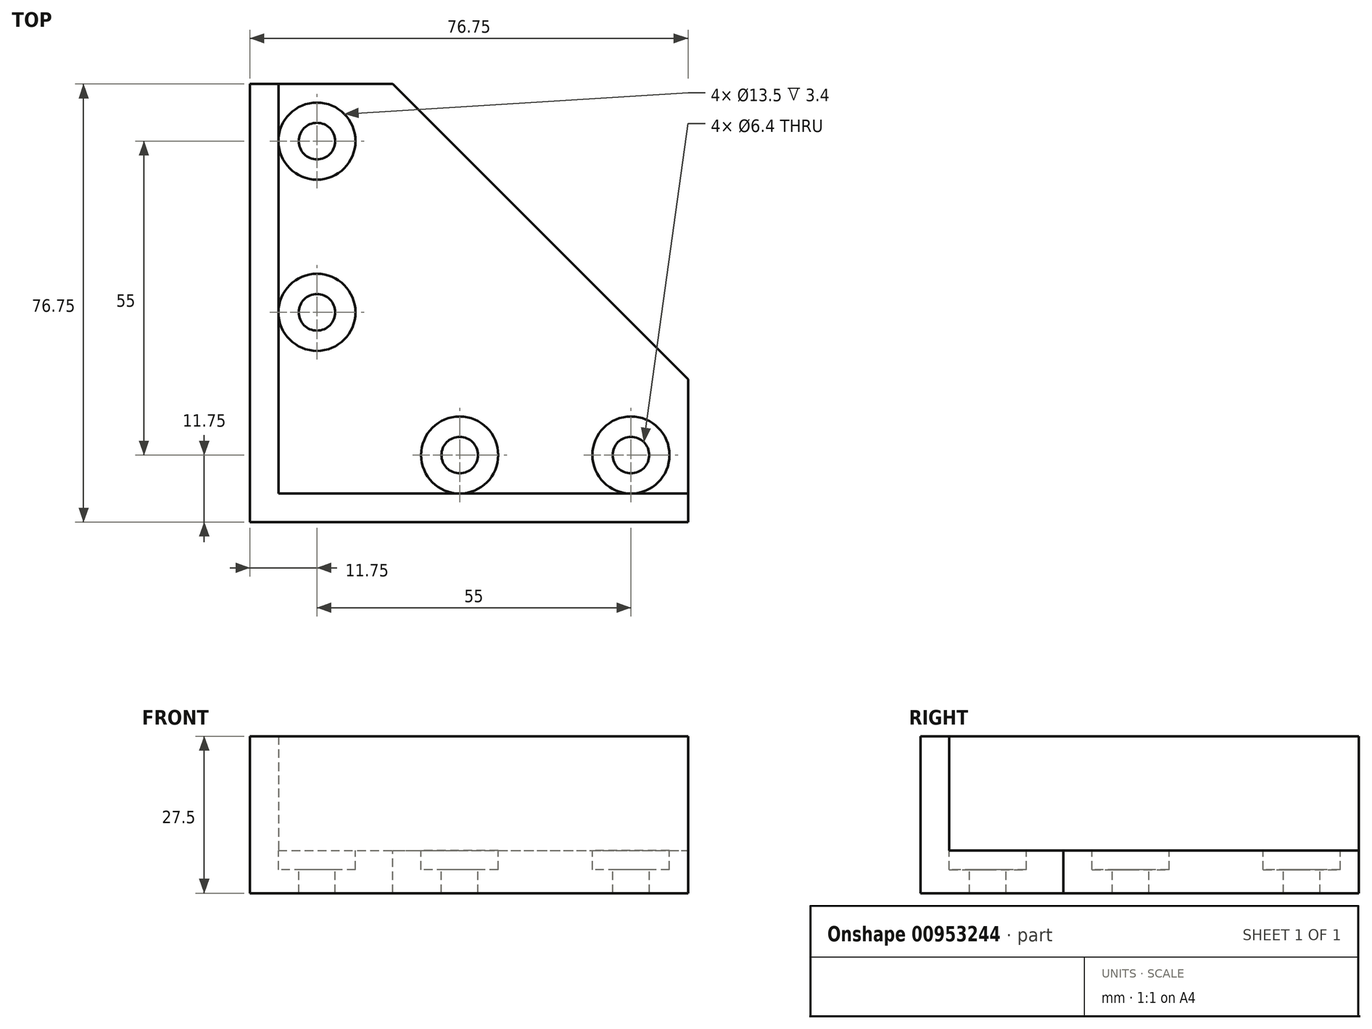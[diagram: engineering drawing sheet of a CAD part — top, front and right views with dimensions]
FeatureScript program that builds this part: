
annotation { "Feature Type Name" : "Feature", "Feature Type Description" : "" }
export const myFeature = defineFeature(function(context is Context, id is Id, definition is map)
    precondition{}
    {
        {
            var Q0;
            Q0=qCreatedBy(makeId("Top.planeOp"),FACE);
            var sketch = newSketch(context, id + "F0", { "sketchPlane" : qUnion([Q0])});
            skCircle(sketch, "E0", {"center": v(0, 55) * mm, "radius": 6.75 * mm});
            skCircle(sketch, "E1", {"center": v(0, 25) * mm, "radius": 6.75 * mm});
            skCircle(sketch, "E2", {"center": v(25, 0) * mm, "radius": 6.75 * mm});
            skCircle(sketch, "E3", {"center": v(55, 0) * mm, "radius": 6.75 * mm});
            skSolve(sketch);
        }
        {
            var Q0;
            Q0=qCreatedBy(makeId("Top.planeOp"),FACE);
            var sketch = newSketch(context, id + "F1", { "sketchPlane" : qUnion([Q0])});
            skLineSegment(sketch, "E4.bottom", {"start": v(-6.75, 65) * mm, "end": v(13.25, 65) * mm});
            skLineSegment(sketch, "E4.top", {"start": v(-6.75, -6.75) * mm, "end": v(13.25, -6.75) * mm});
            skLineSegment(sketch, "E4.left", {"start": v(-6.75, 65) * mm, "end": v(-6.75, -6.75) * mm});
            skLineSegment(sketch, "E4.right", {"start": v(13.25, 65) * mm, "end": v(13.25, -6.75) * mm});
            skLineSegment(sketch, "E5.bottom", {"start": v(13.25, -6.75) * mm, "end": v(65, -6.75) * mm});
            skLineSegment(sketch, "E5.top", {"start": v(13.25, 13.25) * mm, "end": v(65, 13.25) * mm});
            skLineSegment(sketch, "E5.right", {"start": v(65, -6.75) * mm, "end": v(65, 13.25) * mm});
            skLineSegment(sketch, "E6", {"start": v(13.25, 65) * mm, "end": v(65, 13.25) * mm});
            skSolve(sketch);
        }
        {
            var Q0;
            {var subQ1=sQuery(id+"F1.wireOp",EDGE,"E4.bottom");Q0=makeQuery(id+"F1.imprint","IMPRINT",FACE,{"disambiguationData":[TD([[makeQuery(id+"F1.imprint","IMPRINT",EDGE,{"derivedFrom":subQ1}),-1.0]])]});}
            var Q1;
            {var subQ2=sQuery(id+"F1.wireOp",EDGE,"E5.top");Q1=makeQuery(id+"F1.imprint","IMPRINT",FACE,{"disambiguationData":[TD([[makeQuery(id+"F1.imprint","IMPRINT",EDGE,{"derivedFrom":subQ2}),1.0]])]});}
            var Q2;
            {var subQ0=sQuery(id+"F1.wireOp",EDGE,"E5.bottom");Q2=makeQuery(id+"F1.imprint","IMPRINT",FACE,{"disambiguationData":[TD([[makeQuery(id+"F1.imprint","IMPRINT",EDGE,{"derivedFrom":subQ0}),1.0]])]});}
            extrude(context, id + "F2", {"entities" : qUnion([Q0, Q1, Q2]), "oppositeDirection" : true, "depth" : 7.5 * mm, "offsetDistance" : 25 * mm});
        }
        {
            var Q0;
            Q0=makeQuery(id+"F2.opExtrude","CAP_FACE",FACE,{"disambiguationData":[OSD([sQuery(id+"F1.wireOp",EDGE,"E4.bottom"),sQuery(id+"F1.wireOp",EDGE,"E4.top"),sQuery(id+"F1.wireOp",EDGE,"E4.left"),sQuery(id+"F1.wireOp",EDGE,"E5.bottom"),sQuery(id+"F1.wireOp",EDGE,"E5.right"),sQuery(id+"F1.wireOp",EDGE,"E6")])],"isStart":true});
            var sketch = newSketch(context, id + "F3", { "sketchPlane" : qUnion([Q0])});
            skLineSegment(sketch, "E7.bottom", {"start": v(-6.75, 65) * mm, "end": v(-11.75, 65) * mm});
            skLineSegment(sketch, "E7.top", {"start": v(-6.75, -6.75) * mm, "end": v(-11.75, -6.75) * mm});
            skLineSegment(sketch, "E7.left", {"start": v(-6.75, 65) * mm, "end": v(-6.75, -6.75) * mm});
            skLineSegment(sketch, "E7.right", {"start": v(-11.75, 65) * mm, "end": v(-11.75, -6.75) * mm});
            skLineSegment(sketch, "E8.bottom", {"start": v(65, -6.75) * mm, "end": v(-11.75, -6.75) * mm});
            skLineSegment(sketch, "E8.top", {"start": v(65, -11.75) * mm, "end": v(-11.75, -11.75) * mm});
            skLineSegment(sketch, "E8.left", {"start": v(65, -6.75) * mm, "end": v(65, -11.75) * mm});
            skLineSegment(sketch, "E8.right", {"start": v(-11.75, -6.75) * mm, "end": v(-11.75, -11.75) * mm});
            skSolve(sketch);
        }
        {
            var Q0;
            Q0 = qSketchRegion(id + "F3", true);
            extrude(context, id + "F4", {"entities" : qUnion([Q0]), "operationType" : NewBodyOperationType.ADD, "oppositeDirection" : true, "depth" : 7.5 * mm, "offsetDistance" : 25 * mm});
        }
        {
            var Q0;
            Q0=makeQuery(id+"F0.imprint","IMPRINT",FACE,{"disambiguationData":[TD([[makeQuery(id+"F0.imprint","IMPRINT",EDGE,{"derivedFrom":sQuery(id+"F0.wireOp",EDGE,"E3")}),1.0]])]});
            var Q1;
            Q1=makeQuery(id+"F0.imprint","IMPRINT",FACE,{"disambiguationData":[TD([[makeQuery(id+"F0.imprint","IMPRINT",EDGE,{"derivedFrom":sQuery(id+"F0.wireOp",EDGE,"E2")}),1.0]])]});
            var Q2;
            Q2=makeQuery(id+"F0.imprint","IMPRINT",FACE,{"disambiguationData":[TD([[makeQuery(id+"F0.imprint","IMPRINT",EDGE,{"derivedFrom":sQuery(id+"F0.wireOp",EDGE,"E1")}),1.0]])]});
            var Q3;
            Q3=makeQuery(id+"F0.imprint","IMPRINT",FACE,{"disambiguationData":[TD([[makeQuery(id+"F0.imprint","IMPRINT",EDGE,{"derivedFrom":sQuery(id+"F0.wireOp",EDGE,"E0")}),1.0]])]});
            extrude(context, id + "F5", {"entities" : qUnion([Q0, Q1, Q2, Q3]), "operationType" : NewBodyOperationType.REMOVE, "oppositeDirection" : true, "depth" : 3.4 * mm, "offsetDistance" : 25 * mm});
        }
        {
            var Q0;
            Q0=makeQuery(id+"F3.imprint","IMPRINT",FACE,{"disambiguationData":[TD([[makeQuery(id+"F3.imprint","IMPRINT",EDGE,{"derivedFrom":sQuery(id+"F3.wireOp",EDGE,"E7.bottom")}),1.0]])]});
            var Q1;
            Q1=makeQuery(id+"F3.imprint","IMPRINT",FACE,{"disambiguationData":[TD([[makeQuery(id+"F3.imprint","IMPRINT",EDGE,{"derivedFrom":sQuery(id+"F3.wireOp",EDGE,"E8.top")}),-1.0]])]});
            extrude(context, id + "F6", {"entities" : qUnion([Q0, Q1]), "operationType" : NewBodyOperationType.ADD, "depth" : 20 * mm, "offsetDistance" : 25 * mm});
        }
        {
            var Q0;
            {var subQ2=sQuery(id+"F3.wireOp",EDGE,"E7.left");Q0=makeQuery(id+"F3.imprint","IMPRINT",FACE,{"disambiguationData":[TD([[makeQuery(id+"F3.imprint","IMPRINT",EDGE,{"derivedFrom":subQ2}),1.0]])]});}
            var sketch = newSketch(context, id + "F7", { "sketchPlane" : qUnion([Q0])});
            skCircle(sketch, "E9", {"center": v(0, 55) * mm, "radius": 3.2 * mm});
            skCircle(sketch, "E10", {"center": v(0, 25) * mm, "radius": 3.2 * mm});
            skCircle(sketch, "E11", {"center": v(25, 0) * mm, "radius": 3.2 * mm});
            skCircle(sketch, "E12", {"center": v(55, 0) * mm, "radius": 3.2 * mm});
            skSolve(sketch);
        }
        {
            var Q0;
            Q0=makeQuery(id+"F7.imprint","IMPRINT",FACE,{"disambiguationData":[TD([[makeQuery(id+"F7.imprint","IMPRINT",EDGE,{"derivedFrom":sQuery(id+"F7.wireOp",EDGE,"E10")}),1.0]])]});
            var Q1;
            Q1=makeQuery(id+"F7.imprint","IMPRINT",FACE,{"disambiguationData":[TD([[makeQuery(id+"F7.imprint","IMPRINT",EDGE,{"derivedFrom":sQuery(id+"F7.wireOp",EDGE,"E9")}),1.0]])]});
            var Q2;
            Q2=makeQuery(id+"F7.imprint","IMPRINT",FACE,{"disambiguationData":[TD([[makeQuery(id+"F7.imprint","IMPRINT",EDGE,{"derivedFrom":sQuery(id+"F7.wireOp",EDGE,"E11")}),1.0]])]});
            var Q3;
            Q3=makeQuery(id+"F7.imprint","IMPRINT",FACE,{"disambiguationData":[TD([[makeQuery(id+"F7.imprint","IMPRINT",EDGE,{"derivedFrom":sQuery(id+"F7.wireOp",EDGE,"E12")}),1.0]])]});
            extrude(context, id + "F8", {"entities" : qUnion([Q0, Q1, Q2, Q3]), "operationType" : NewBodyOperationType.REMOVE, "oppositeDirection" : true, "depth" : 25 * mm, "offsetDistance" : 25 * mm});
        }
    });
